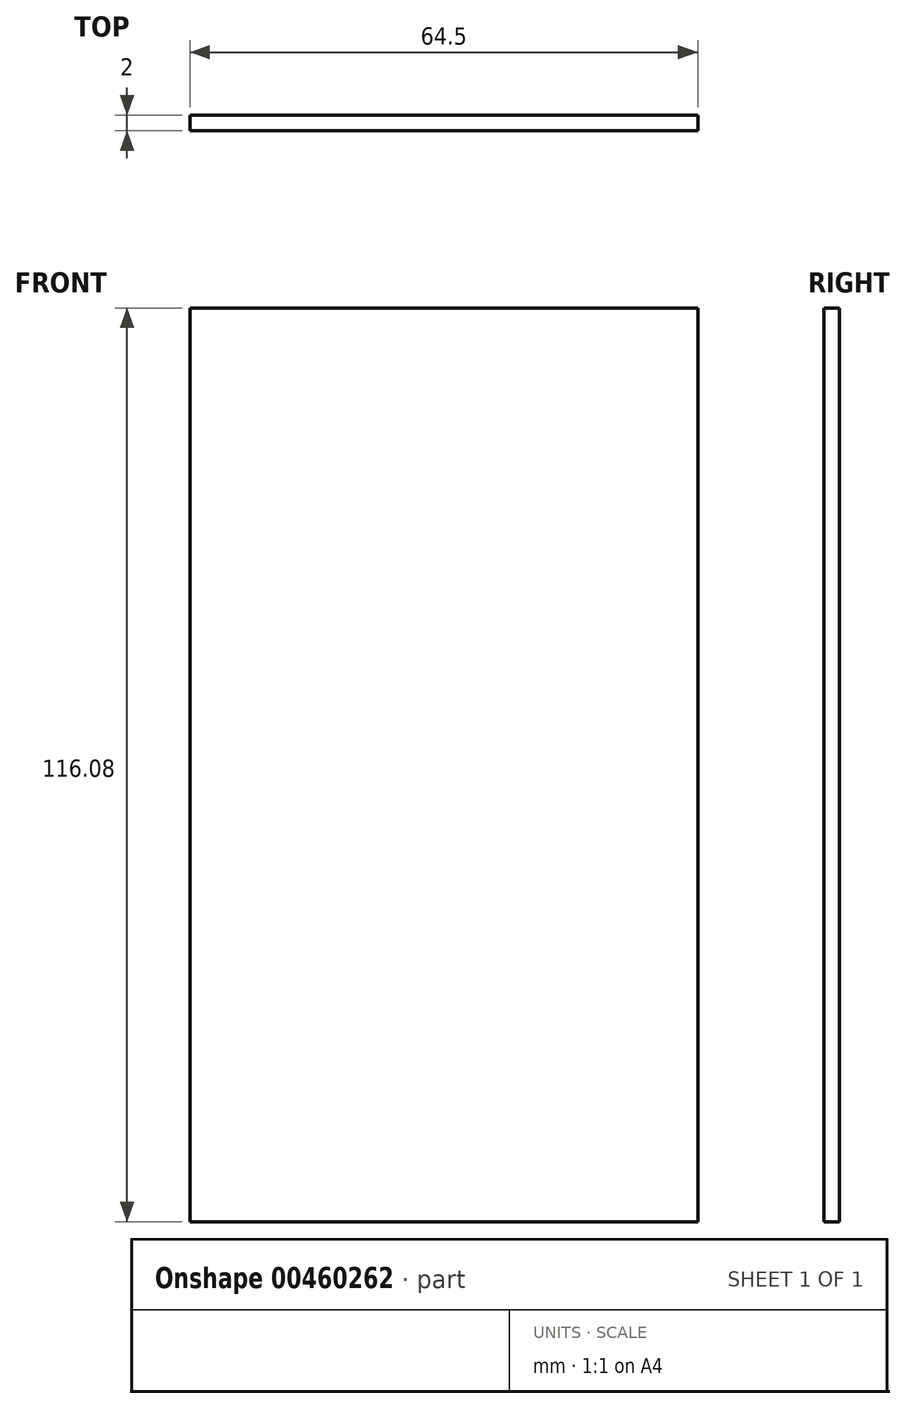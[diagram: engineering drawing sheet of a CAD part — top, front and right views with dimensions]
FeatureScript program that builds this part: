
annotation { "Feature Type Name" : "Feature", "Feature Type Description" : "" }
export const myFeature = defineFeature(function(context is Context, id is Id, definition is map)
    precondition{}
    {
        {
            var Q0;
            Q0=qCreatedBy(makeId("Front.planeOp"),FACE);
            var sketch = newSketch(context, id + "F0", { "sketchPlane" : qUnion([Q0])});
            skLineSegment(sketch, "E0.bottom", {"start": v(32.25, -58.04) * mm, "end": v(-32.25, -58.04) * mm});
            skLineSegment(sketch, "E0.top", {"start": v(32.25, 58.04) * mm, "end": v(-32.25, 58.04) * mm});
            skLineSegment(sketch, "E0.left", {"start": v(32.25, -58.04) * mm, "end": v(32.25, 58.04) * mm});
            skLineSegment(sketch, "E0.right", {"start": v(-32.25, -58.04) * mm, "end": v(-32.25, 58.04) * mm});
            skPoint(sketch, "E0.middle", {"position": v(0, 0) * mm});
            skSolve(sketch);
        }
        {
            var Q0;
            Q0 = qSketchRegion(id + "F0", true);
            extrude(context, id + "F1", {"entities" : qUnion([Q0]), "oppositeDirection" : true, "depth" : 2 * mm});
        }
    });
